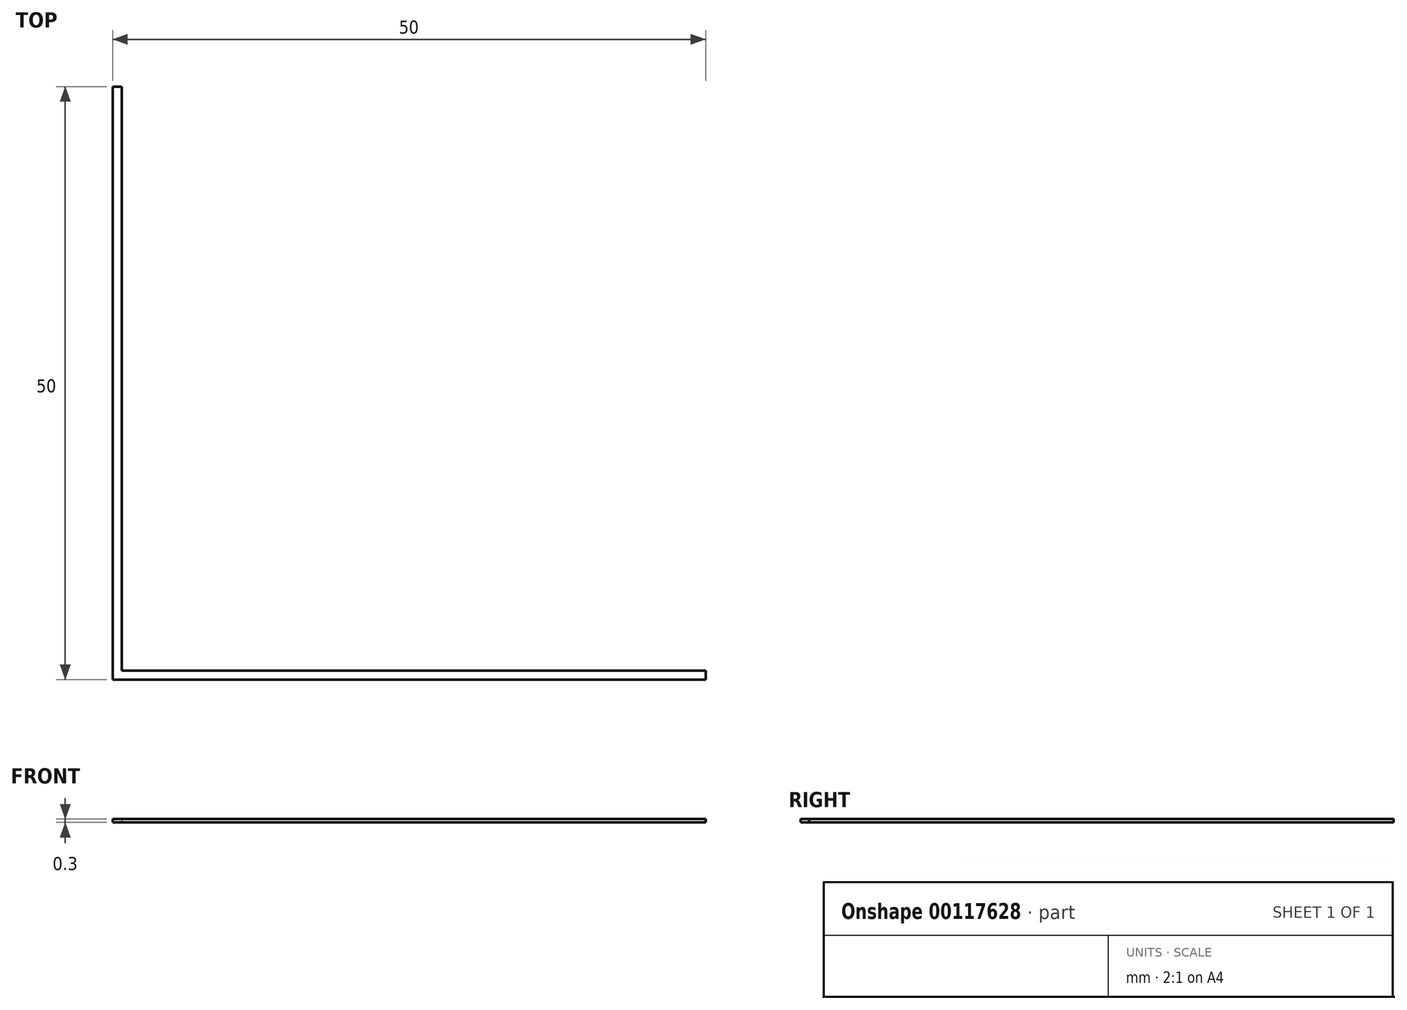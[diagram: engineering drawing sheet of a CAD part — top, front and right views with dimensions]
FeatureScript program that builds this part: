
annotation { "Feature Type Name" : "Feature", "Feature Type Description" : "" }
export const myFeature = defineFeature(function(context is Context, id is Id, definition is map)
    precondition{}
    {
        {
            var Q0;
            Q0=qCreatedBy(makeId("Top.planeOp"),FACE);
            var sketch = newSketch(context, id + "F0", { "sketchPlane" : qUnion([Q0])});
            skLineSegment(sketch, "E0", {"start": v(0, 0) * mm, "end": v(0, 50) * mm});
            skLineSegment(sketch, "E1", {"start": v(0, 50) * mm, "end": v(0.75, 50) * mm});
            skLineSegment(sketch, "E2", {"start": v(0.75, 50) * mm, "end": v(0.75, 0.75) * mm});
            skLineSegment(sketch, "E3", {"start": v(0.75, 0.75) * mm, "end": v(50, 0.75) * mm});
            skLineSegment(sketch, "E4", {"start": v(50, 0.75) * mm, "end": v(50, 0) * mm});
            skLineSegment(sketch, "E5", {"start": v(50, 0) * mm, "end": v(0, 0) * mm});
            skSolve(sketch);
        }
        {
            var Q0;
            Q0=makeQuery(id+"F0.imprint","IMPRINT",FACE,{"disambiguationData":[TD([[makeQuery(id+"F0.imprint","IMPRINT",EDGE,{"derivedFrom":sQuery(id+"F0.wireOp",EDGE,"E0")}),-1.0]])]});
            extrude(context, id + "F1", {"entities" : qUnion([Q0]), "depth" : 0.3 * mm});
        }
    });
